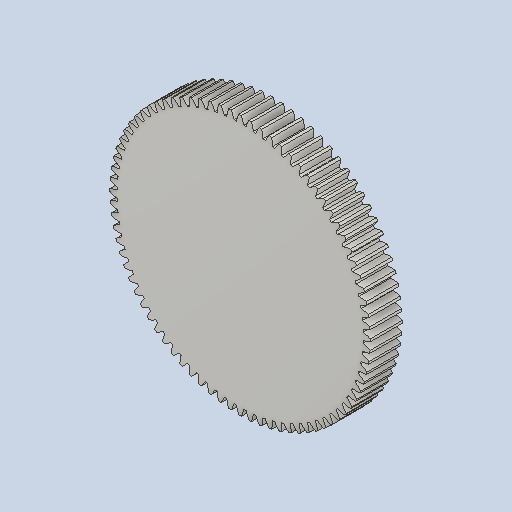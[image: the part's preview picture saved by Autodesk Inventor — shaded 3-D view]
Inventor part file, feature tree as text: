
AUTODESK INVENTOR PART (.ipt)
format: ipt  version: 2023 (Build 270158030, 158C)  size: 432,640 bytes
history: native  units: mm (DEFAULTED — no unit token found)
features: plane x3, other x3, sketch x2, extrude x1
ambient origin geometry x8: Origin, YZ Plane, XZ Plane, XY Plane, X Axis, Y Axis, Z Axis, Center Point
bodies: Solid1 (feature_tree)
feature tree (9):
  extrude  "Extrusion1"  Depth=20.0mm TaperAngle=0.0deg
  plane  "Work Plane2"
  plane  "Work Plane8"
  plane  "Work Plane9"
  other  "Spur Gear"
  sketch  "Sketch1"  dims[d0=164.0mm d1=20.0mm d2=0.0mm]
  sketch  "Sketch2"  dims[d3=160.0mm d4=10.0mm d5=0.0mm d16=100.0mm d17=0.0mm d34=0.392699mm d39=0.0mm d41=0.0mm d43=100.0mm d46=100.0mm d47=0.0mm d48=0.0mm]
  other  "Srf1"
  other  "Pitch Diameter"
